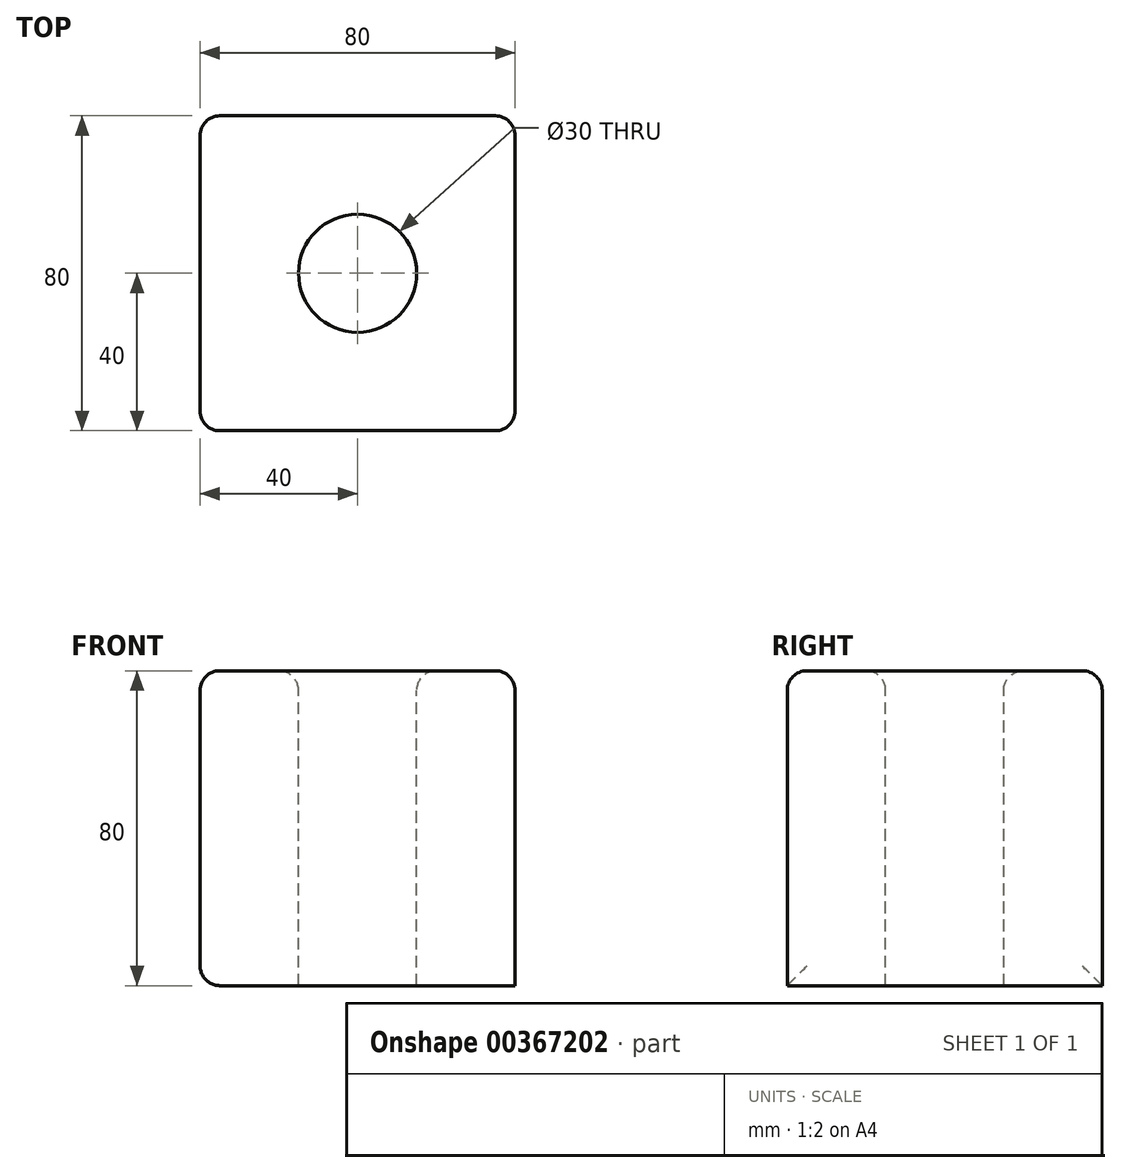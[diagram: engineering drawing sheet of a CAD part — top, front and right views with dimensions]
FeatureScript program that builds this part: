
annotation { "Feature Type Name" : "Feature", "Feature Type Description" : "" }
export const myFeature = defineFeature(function(context is Context, id is Id, definition is map)
    precondition{}
    {
        {
            var Q0;
            Q0=qCreatedBy(makeId("Top.planeOp"),FACE);
            var sketch = newSketch(context, id + "F0", { "sketchPlane" : qUnion([Q0])});
            skLineSegment(sketch, "E0.bottom", {"start": v(-40, 40) * mm, "end": v(40, 40) * mm});
            skLineSegment(sketch, "E0.top", {"start": v(-40, -40) * mm, "end": v(40, -40) * mm});
            skLineSegment(sketch, "E0.left", {"start": v(-40, 40) * mm, "end": v(-40, -40) * mm});
            skLineSegment(sketch, "E0.right", {"start": v(40, 40) * mm, "end": v(40, -40) * mm});
            skPoint(sketch, "E0.middle", {"position": v(0, 0) * mm});
            skSolve(sketch);
        }
        {
            var Q0;
            Q0=makeQuery(id+"F0.imprint","IMPRINT",FACE,{"disambiguationData":[TD([[makeQuery(id+"F0.imprint","IMPRINT",EDGE,{"derivedFrom":sQuery(id+"F0.wireOp",EDGE,"E0.bottom")}),-1.0]])]});
            extrude(context, id + "F1", {"entities" : qUnion([Q0]), "depth" : 80 * mm});
        }
        {
            var Q0;
            Q0=makeQuery(id+"F1.opExtrude","CAP_FACE",FACE,{"disambiguationData":[OSD([sQuery(id+"F0.wireOp",EDGE,"E0.bottom"),sQuery(id+"F0.wireOp",EDGE,"E0.top"),sQuery(id+"F0.wireOp",EDGE,"E0.left"),sQuery(id+"F0.wireOp",EDGE,"E0.right")])],"isStart":false});
            var sketch = newSketch(context, id + "F2", { "sketchPlane" : qUnion([Q0])});
            skCircle(sketch, "E1", {"center": v(0, 0) * mm, "radius": 15 * mm});
            skSolve(sketch);
        }
        {
            var Q0;
            Q0=makeQuery(id+"F2.imprint","IMPRINT",FACE,{"disambiguationData":[TD([[makeQuery(id+"F2.imprint","IMPRINT",EDGE,{"derivedFrom":sQuery(id+"F2.wireOp",EDGE,"E1")}),1.0]])]});
            extrude(context, id + "F3", {"entities" : qUnion([Q0]), "operationType" : NewBodyOperationType.REMOVE, "endBound" : BoundingType.THROUGH_ALL, "oppositeDirection" : true, "depth" : 25 * mm});
        }
        {
            var Q0;
            Q0=makeQuery(id+"F1.opExtrude","CAP_EDGE",EDGE,{"disambiguationData":[OSD([sQuery(id+"F0.wireOp",EDGE,"E0.bottom")])],"isStart":false});
            var Q1;
            Q1=makeQuery(id+"F1.opExtrude","CAP_EDGE",EDGE,{"disambiguationData":[OSD([sQuery(id+"F0.wireOp",EDGE,"E0.left")])],"isStart":false});
            var Q2;
            Q2=makeQuery(id+"F1.opExtrude","SWEPT_EDGE",EDGE,{"disambiguationData":[OSD([sQuery(id+"F0.wireOp",EDGE,"E0.bottom"),sQuery(id+"F0.wireOp",EDGE,"E0.left")])]});
            var Q3;
            Q3=makeQuery(id+"F1.opExtrude","SWEPT_EDGE",EDGE,{"disambiguationData":[OSD([sQuery(id+"F0.wireOp",EDGE,"E0.bottom"),sQuery(id+"F0.wireOp",EDGE,"E0.right")])]});
            var Q4;
            Q4=makeQuery(id+"F1.opExtrude","CAP_FACE",FACE,{"disambiguationData":[OSD([sQuery(id+"F0.wireOp",EDGE,"E0.bottom"),sQuery(id+"F0.wireOp",EDGE,"E0.top"),sQuery(id+"F0.wireOp",EDGE,"E0.left"),sQuery(id+"F0.wireOp",EDGE,"E0.right")])],"isStart":false});
            var Q5;
            Q5=makeQuery(id+"F1.opExtrude","SWEPT_EDGE",EDGE,{"disambiguationData":[OSD([sQuery(id+"F0.wireOp",EDGE,"E0.top"),sQuery(id+"F0.wireOp",EDGE,"E0.left")])]});
            var Q6;
            Q6=makeQuery(id+"F1.opExtrude","CAP_EDGE",EDGE,{"disambiguationData":[OSD([sQuery(id+"F0.wireOp",EDGE,"E0.left")])],"isStart":true});
            var Q7;
            Q7=makeQuery(id+"F1.opExtrude","SWEPT_EDGE",EDGE,{"disambiguationData":[OSD([sQuery(id+"F0.wireOp",EDGE,"E0.top"),sQuery(id+"F0.wireOp",EDGE,"E0.right")])]});
            fillet(context, id + "F4", {"entities" : qUnion([Q0, Q1, Q2, Q3, Q4, Q5, Q6, Q7]), "radius" : 5 * mm, "tangentPropagation" : true, "allowEdgeOverflow" : false});
        }
    });
